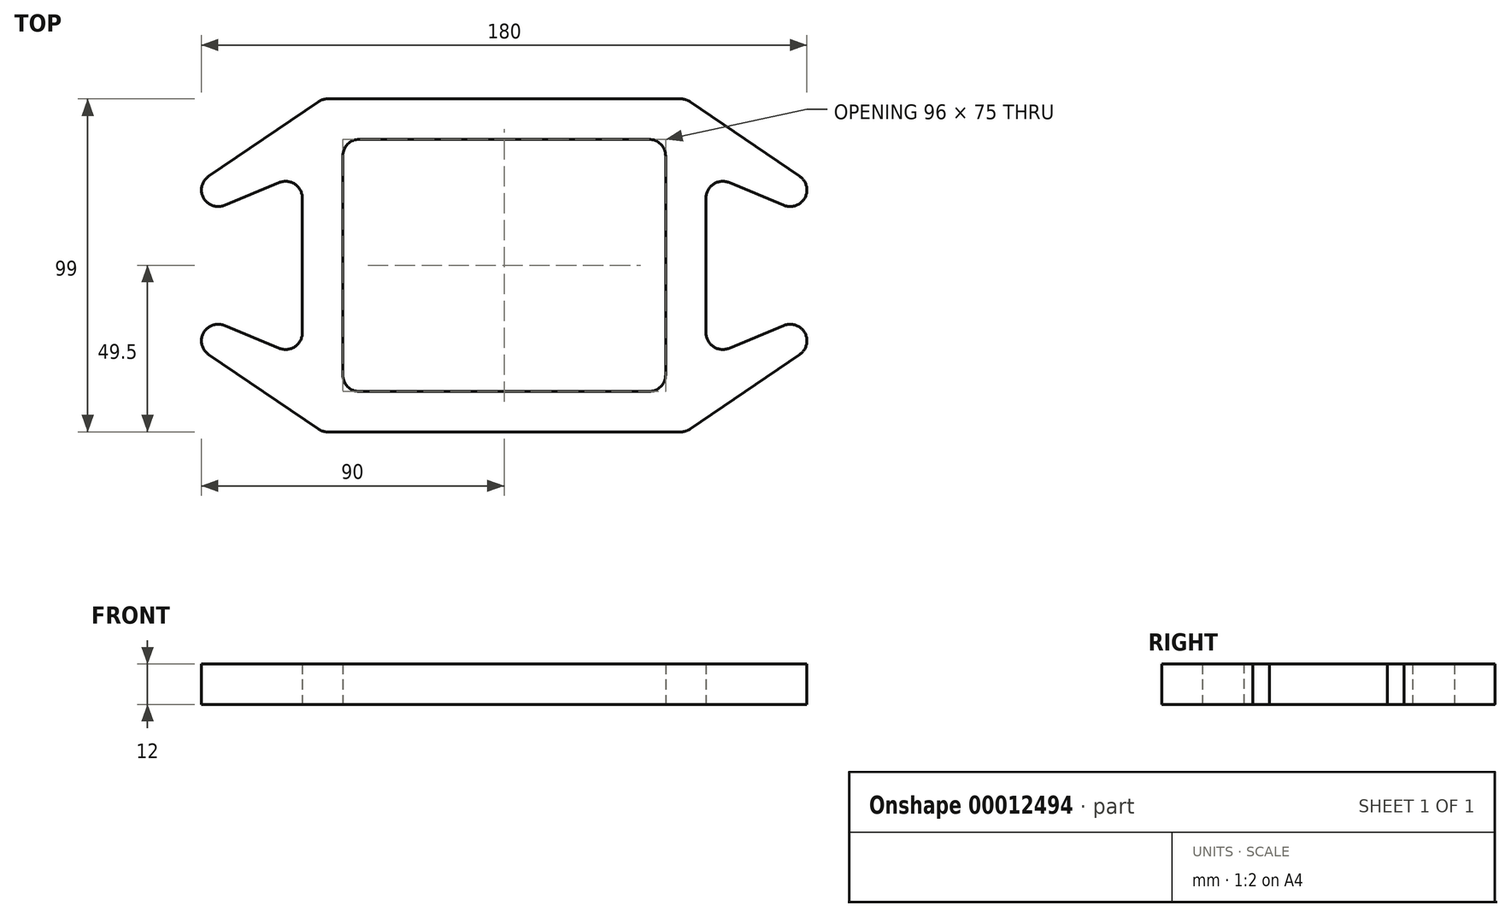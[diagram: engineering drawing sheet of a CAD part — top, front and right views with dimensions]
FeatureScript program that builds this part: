
annotation { "Feature Type Name" : "Feature", "Feature Type Description" : "" }
export const myFeature = defineFeature(function(context is Context, id is Id, definition is map)
    precondition{}
    {
        {
            var Q0;
            Q0=qCreatedBy(makeId("Top.planeOp"),FACE);
            var sketch = newSketch(context, id + "F0", { "sketchPlane" : qUnion([Q0])});
            skLineSegment(sketch, "E0.rect.bottom", {"start": v(54, 49.5) * mm, "end": v(-54, 49.5) * mm});
            skLineSegment(sketch, "E0.rect.top", {"start": v(54, -49.5) * mm, "end": v(-54, -49.5) * mm});
            skLineSegment(sketch, "E0.rect.left", {"start": v(90, 25) * mm, "end": v(90, 15) * mm});
            skLineSegment(sketch, "E0.rect.right", {"start": v(-90, 25) * mm, "end": v(-90, 15) * mm});
            skPoint(sketch, "E0.rect.middle", {"position": v(0, 0) * mm});
            skLineSegment(sketch, "E1", {"start": v(-90, -25) * mm, "end": v(-54, -49.5) * mm});
            skLineSegment(sketch, "E2.0.MirrorCS", {"start": v(-90, 25) * mm, "end": v(-54, 49.5) * mm});
            skLineSegment(sketch, "E3.0.MirrorCS", {"start": v(90, 25) * mm, "end": v(54, 49.5) * mm});
            skLineSegment(sketch, "E4.0.MirrorCS", {"start": v(90, -25) * mm, "end": v(54, -49.5) * mm});
            skPoint(sketch, "E5.orphan", {"position": v(90, 49.5) * mm});
            skPoint(sketch, "E6.orphan", {"position": v(90, -49.5) * mm});
            skPoint(sketch, "E7.orphan", {"position": v(-90, -49.5) * mm});
            skPoint(sketch, "E8.orphan", {"position": v(-90, 49.5) * mm});
            skLineSegment(sketch, "E9", {"start": v(-90, -15) * mm, "end": v(-60, -27.5) * mm});
            skLineSegment(sketch, "E10", {"start": v(-60, -27.5) * mm, "end": v(-60, 0) * mm});
            skLineSegment(sketch, "E11.0.MirrorCS", {"start": v(-60, 27.5) * mm, "end": v(-60, 0) * mm});
            skLineSegment(sketch, "E12.0.MirrorCS", {"start": v(-90, 15) * mm, "end": v(-60, 27.5) * mm});
            skLineSegment(sketch, "E13.0.MirrorCS", {"start": v(90, 15) * mm, "end": v(60, 27.5) * mm});
            skLineSegment(sketch, "E14.0.MirrorCS", {"start": v(60, 27.5) * mm, "end": v(60, 0) * mm});
            skLineSegment(sketch, "E15.0.MirrorCS", {"start": v(60, -27.5) * mm, "end": v(60, 0) * mm});
            skLineSegment(sketch, "E16.0.MirrorCS", {"start": v(90, -15) * mm, "end": v(60, -27.5) * mm});
            skLineSegment(sketch, "E17.trimOffspring", {"start": v(-90, -15) * mm, "end": v(-90, -25) * mm});
            skLineSegment(sketch, "E18.trimOffspring", {"start": v(90, -15) * mm, "end": v(90, -25) * mm});
            skLineSegment(sketch, "E19.rect.bottom", {"start": v(48, 37.5) * mm, "end": v(-48, 37.5) * mm});
            skLineSegment(sketch, "E19.rect.top", {"start": v(48, -37.5) * mm, "end": v(-48, -37.5) * mm});
            skLineSegment(sketch, "E19.rect.left", {"start": v(48, 37.5) * mm, "end": v(48, -37.5) * mm});
            skLineSegment(sketch, "E19.rect.right", {"start": v(-48, 37.5) * mm, "end": v(-48, -37.5) * mm});
            skSolve(sketch);
        }
        {
            var Q0;
            Q0 = qSketchRegion(id + "F0", true);
            var Q1;
            Q1=makeQuery(id+"F0.imprint","IMPRINT",FACE,{"disambiguationData":[TD([[makeQuery(id+"F0.imprint","IMPRINT",EDGE,{"derivedFrom":sQuery(id+"F0.wireOp",EDGE,"E0.rect.bottom")}),1.0]])]});
            extrude(context, id + "F1", {"entities" : qUnion([Q0, Q1]), "depth" : 12 * mm});
        }
        {
            var Q0;
            Q0=makeQuery(id+"F1.opExtrude","SWEPT_EDGE",EDGE,{"disambiguationData":[OSD([sQuery(id+"F0.wireOp",EDGE,"E0.rect.left"),sQuery(id+"F0.wireOp",EDGE,"E13.0.MirrorCS")])]});
            var Q1;
            Q1=makeQuery(id+"F1.opExtrude","SWEPT_EDGE",EDGE,{"disambiguationData":[OSD([sQuery(id+"F0.wireOp",EDGE,"E13.0.MirrorCS"),sQuery(id+"F0.wireOp",EDGE,"E14.0.MirrorCS")])]});
            var Q2;
            Q2=makeQuery(id+"F1.opExtrude","SWEPT_EDGE",EDGE,{"disambiguationData":[OSD([sQuery(id+"F0.wireOp",EDGE,"E0.rect.left"),sQuery(id+"F0.wireOp",EDGE,"E3.0.MirrorCS")])]});
            var Q3;
            Q3=makeQuery(id+"F1.opExtrude","SWEPT_EDGE",EDGE,{"disambiguationData":[OSD([sQuery(id+"F0.wireOp",EDGE,"E0.rect.bottom"),sQuery(id+"F0.wireOp",EDGE,"E3.0.MirrorCS")])]});
            var Q4;
            Q4=makeQuery(id+"F1.opExtrude","SWEPT_EDGE",EDGE,{"disambiguationData":[OSD([sQuery(id+"F0.wireOp",EDGE,"E15.0.MirrorCS"),sQuery(id+"F0.wireOp",EDGE,"E16.0.MirrorCS")])]});
            var Q5;
            Q5=makeQuery(id+"F1.opExtrude","SWEPT_EDGE",EDGE,{"disambiguationData":[OSD([sQuery(id+"F0.wireOp",EDGE,"E16.0.MirrorCS"),sQuery(id+"F0.wireOp",EDGE,"E18.trimOffspring")])]});
            var Q6;
            Q6=makeQuery(id+"F1.opExtrude","SWEPT_EDGE",EDGE,{"disambiguationData":[OSD([sQuery(id+"F0.wireOp",EDGE,"E4.0.MirrorCS"),sQuery(id+"F0.wireOp",EDGE,"E18.trimOffspring")])]});
            var Q7;
            Q7=makeQuery(id+"F1.opExtrude","SWEPT_EDGE",EDGE,{"disambiguationData":[OSD([sQuery(id+"F0.wireOp",EDGE,"E0.rect.top"),sQuery(id+"F0.wireOp",EDGE,"E4.0.MirrorCS")])]});
            var Q8;
            Q8=makeQuery(id+"F1.opExtrude","SWEPT_EDGE",EDGE,{"disambiguationData":[OSD([sQuery(id+"F0.wireOp",EDGE,"E0.rect.top"),sQuery(id+"F0.wireOp",EDGE,"E1")])]});
            var Q9;
            Q9=makeQuery(id+"F1.opExtrude","SWEPT_EDGE",EDGE,{"disambiguationData":[OSD([sQuery(id+"F0.wireOp",EDGE,"E1"),sQuery(id+"F0.wireOp",EDGE,"E17.trimOffspring")])]});
            var Q10;
            Q10=makeQuery(id+"F1.opExtrude","SWEPT_EDGE",EDGE,{"disambiguationData":[OSD([sQuery(id+"F0.wireOp",EDGE,"E0.rect.right"),sQuery(id+"F0.wireOp",EDGE,"E12.0.MirrorCS")])]});
            var Q11;
            Q11=makeQuery(id+"F1.opExtrude","SWEPT_EDGE",EDGE,{"disambiguationData":[OSD([sQuery(id+"F0.wireOp",EDGE,"E19.rect.bottom"),sQuery(id+"F0.wireOp",EDGE,"E19.rect.right")])]});
            var Q12;
            Q12=makeQuery(id+"F1.opExtrude","SWEPT_EDGE",EDGE,{"disambiguationData":[OSD([sQuery(id+"F0.wireOp",EDGE,"E19.rect.bottom"),sQuery(id+"F0.wireOp",EDGE,"E19.rect.left")])]});
            var Q13;
            Q13=makeQuery(id+"F1.opExtrude","SWEPT_EDGE",EDGE,{"disambiguationData":[OSD([sQuery(id+"F0.wireOp",EDGE,"E11.0.MirrorCS"),sQuery(id+"F0.wireOp",EDGE,"E12.0.MirrorCS")])]});
            var Q14;
            Q14=makeQuery(id+"F1.opExtrude","SWEPT_EDGE",EDGE,{"disambiguationData":[OSD([sQuery(id+"F0.wireOp",EDGE,"E0.rect.right"),sQuery(id+"F0.wireOp",EDGE,"E2.0.MirrorCS")])]});
            var Q15;
            Q15=makeQuery(id+"F1.opExtrude","SWEPT_EDGE",EDGE,{"disambiguationData":[OSD([sQuery(id+"F0.wireOp",EDGE,"E9"),sQuery(id+"F0.wireOp",EDGE,"E17.trimOffspring")])]});
            var Q16;
            Q16=makeQuery(id+"F1.opExtrude","SWEPT_EDGE",EDGE,{"disambiguationData":[OSD([sQuery(id+"F0.wireOp",EDGE,"E19.rect.top"),sQuery(id+"F0.wireOp",EDGE,"E19.rect.right")])]});
            var Q17;
            Q17=makeQuery(id+"F1.opExtrude","SWEPT_EDGE",EDGE,{"disambiguationData":[OSD([sQuery(id+"F0.wireOp",EDGE,"E19.rect.top"),sQuery(id+"F0.wireOp",EDGE,"E19.rect.left")])]});
            var Q18;
            Q18=makeQuery(id+"F1.opExtrude","SWEPT_EDGE",EDGE,{"disambiguationData":[OSD([sQuery(id+"F0.wireOp",EDGE,"E0.rect.bottom"),sQuery(id+"F0.wireOp",EDGE,"E2.0.MirrorCS")])]});
            var Q19;
            Q19=makeQuery(id+"F1.opExtrude","SWEPT_EDGE",EDGE,{"disambiguationData":[OSD([sQuery(id+"F0.wireOp",EDGE,"E9"),sQuery(id+"F0.wireOp",EDGE,"E10")])]});
            fillet(context, id + "F2", {"entities" : qUnion([Q0, Q1, Q2, Q3, Q4, Q5, Q6, Q7, Q8, Q9, Q10, Q11, Q12, Q13, Q14, Q15, Q16, Q17, Q18, Q19]), "radius" : 5 * mm, "tangentPropagation" : true, "allowEdgeOverflow" : false});
        }
    });
